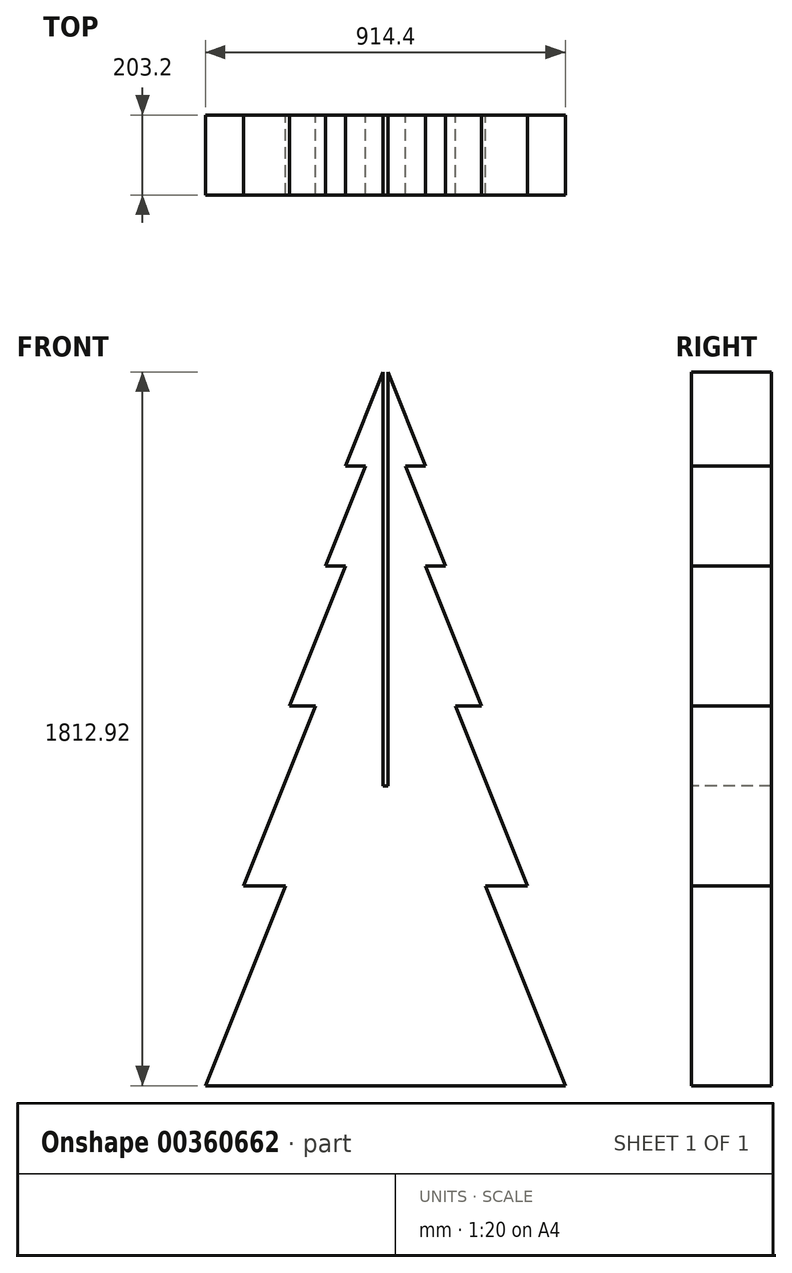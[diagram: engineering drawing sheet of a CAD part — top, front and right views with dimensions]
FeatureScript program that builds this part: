
annotation { "Feature Type Name" : "Feature", "Feature Type Description" : "" }
export const myFeature = defineFeature(function(context is Context, id is Id, definition is map)
    precondition{}
    {
        {
            var Q0;
            Q0=qCreatedBy(makeId("Front.planeOp"),FACE);
            var sketch = newSketch(context, id + "F0", { "sketchPlane" : qUnion([Q0])});
            skLineSegment(sketch, "E0.bottom", {"start": v(457.2, 0) * mm, "end": v(-457.2, 0) * mm, "construction": true});
            skLineSegment(sketch, "E1", {"start": v(0, 0) * mm, "end": v(0, 1828.8) * mm, "construction": true});
            skPoint(sketch, "E1.endSnap0", {"position": v(0, 1828.8) * mm});
            skLineSegment(sketch, "E2", {"start": v(0, 1828.8) * mm, "end": v(-101.6, 1574.8) * mm});
            skLineSegment(sketch, "E3", {"start": v(-101.6, 1574.8) * mm, "end": v(-50.8, 1574.8) * mm});
            skLineSegment(sketch, "E4", {"start": v(-50.8, 1574.8) * mm, "end": v(-152.4, 1320.8) * mm});
            skLineSegment(sketch, "E5", {"start": v(-152.4, 1320.8) * mm, "end": v(-101.6, 1320.8) * mm});
            skLineSegment(sketch, "E6", {"start": v(-101.6, 1320.8) * mm, "end": v(-243.84, 965.2) * mm});
            skLineSegment(sketch, "E7", {"start": v(-243.84, 965.2) * mm, "end": v(-177.8, 965.2) * mm});
            skLineSegment(sketch, "E8", {"start": v(-177.8, 965.2) * mm, "end": v(-360.68, 508) * mm});
            skLineSegment(sketch, "E9", {"start": v(-360.68, 508) * mm, "end": v(-254, 508) * mm});
            skLineSegment(sketch, "E10", {"start": v(-254, 508) * mm, "end": v(-457.2, 0) * mm});
            skLineSegment(sketch, "E11", {"start": v(-457.2, 0) * mm, "end": v(457.2, 0) * mm});
            skLineSegment(sketch, "E12.MirrorCS", {"start": v(0, 1828.8) * mm, "end": v(101.6, 1574.8) * mm});
            skLineSegment(sketch, "E13.MirrorCS", {"start": v(101.6, 1574.8) * mm, "end": v(50.8, 1574.8) * mm});
            skLineSegment(sketch, "E14.MirrorCS", {"start": v(50.8, 1574.8) * mm, "end": v(152.4, 1320.8) * mm});
            skLineSegment(sketch, "E15.MirrorCS", {"start": v(152.4, 1320.8) * mm, "end": v(101.6, 1320.8) * mm});
            skLineSegment(sketch, "E16.MirrorCS", {"start": v(101.6, 1320.8) * mm, "end": v(243.84, 965.2) * mm});
            skLineSegment(sketch, "E17.MirrorCS", {"start": v(243.84, 965.2) * mm, "end": v(177.8, 965.2) * mm});
            skLineSegment(sketch, "E18.MirrorCS", {"start": v(177.8, 965.2) * mm, "end": v(360.68, 508) * mm});
            skLineSegment(sketch, "E19.MirrorCS", {"start": v(360.68, 508) * mm, "end": v(254, 508) * mm});
            skLineSegment(sketch, "E20.MirrorCS", {"start": v(254, 508) * mm, "end": v(457.2, 0) * mm});
            skLineSegment(sketch, "E21.bottom", {"start": v(-457.2, 0) * mm, "end": v(762, 0) * mm, "construction": true});
            skLineSegment(sketch, "E21.top", {"start": v(-457.2, 2438.4) * mm, "end": v(762, 2438.4) * mm, "construction": true});
            skLineSegment(sketch, "E21.left", {"start": v(-457.2, 0) * mm, "end": v(-457.2, 2438.4) * mm, "construction": true});
            skLineSegment(sketch, "E21.right", {"start": v(762, 0) * mm, "end": v(762, 2438.4) * mm, "construction": true});
            skSolve(sketch);
        }
        {
            var Q0;
            Q0 = qSketchRegion(id + "F0", true);
            extrude(context, id + "F1", {"entities" : qUnion([Q0]), "depth" : 203.2 * mm});
        }
        {
            var Q0;
            Q0=makeQuery(id+"F1.opExtrude","CAP_FACE",FACE,{"disambiguationData":[OSD([sQuery(id+"F0.wireOp",EDGE,"E2"),sQuery(id+"F0.wireOp",EDGE,"E3"),sQuery(id+"F0.wireOp",EDGE,"E4"),sQuery(id+"F0.wireOp",EDGE,"E5"),sQuery(id+"F0.wireOp",EDGE,"E6"),sQuery(id+"F0.wireOp",EDGE,"E7"),sQuery(id+"F0.wireOp",EDGE,"E8"),sQuery(id+"F0.wireOp",EDGE,"E9"),sQuery(id+"F0.wireOp",EDGE,"E10"),sQuery(id+"F0.wireOp",EDGE,"E11"),sQuery(id+"F0.wireOp",EDGE,"E12.MirrorCS"),sQuery(id+"F0.wireOp",EDGE,"E13.MirrorCS"),sQuery(id+"F0.wireOp",EDGE,"E14.MirrorCS"),sQuery(id+"F0.wireOp",EDGE,"E15.MirrorCS"),sQuery(id+"F0.wireOp",EDGE,"E16.MirrorCS"),sQuery(id+"F0.wireOp",EDGE,"E17.MirrorCS"),sQuery(id+"F0.wireOp",EDGE,"E18.MirrorCS"),sQuery(id+"F0.wireOp",EDGE,"E19.MirrorCS"),sQuery(id+"F0.wireOp",EDGE,"E20.MirrorCS")])],"isStart":false});
            var sketch = newSketch(context, id + "F2", { "sketchPlane" : qUnion([Q0])});
            skLineSegment(sketch, "E22.bottom", {"start": v(6.35, 0) * mm, "end": v(-6.35, 0) * mm});
            skLineSegment(sketch, "E22.top", {"start": v(6.35, 762) * mm, "end": v(-6.35, 762) * mm});
            skLineSegment(sketch, "E22.left", {"start": v(6.35, 0) * mm, "end": v(6.35, 762) * mm});
            skLineSegment(sketch, "E22.right", {"start": v(-6.35, 0) * mm, "end": v(-6.35, 762) * mm});
            skPoint(sketch, "E22.middle", {"position": v(0, 381) * mm});
            skSolve(sketch);
        }
        {
            var Q0;
            Q0=makeQuery(id+"F2.imprint","IMPRINT",FACE,{"disambiguationData":[TD([[makeQuery(id+"F2.imprint","IMPRINT",EDGE,{"derivedFrom":sQuery(id+"F2.wireOp",EDGE,"E22.top")}),-1.0]])]});
            var sketch = newSketch(context, id + "F3", { "sketchPlane" : qUnion([Q0])});
            skLineSegment(sketch, "E23.bottom", {"start": v(-6.35, 762) * mm, "end": v(6.35, 762) * mm});
            skLineSegment(sketch, "E23.top", {"start": v(-6.35, 1905) * mm, "end": v(6.35, 1905) * mm});
            skLineSegment(sketch, "E23.left", {"start": v(-6.35, 762) * mm, "end": v(-6.35, 1905) * mm});
            skLineSegment(sketch, "E23.right", {"start": v(6.35, 762) * mm, "end": v(6.35, 1905) * mm});
            skSolve(sketch);
        }
        {
            var Q0;
            Q0 = qSketchRegion(id + "F3", true);
            extrude(context, id + "F4", {"entities" : qUnion([Q0]), "operationType" : NewBodyOperationType.REMOVE, "endBound" : BoundingType.THROUGH_ALL, "oppositeDirection" : true, "depth" : 25.4 * mm});
        }
    });
